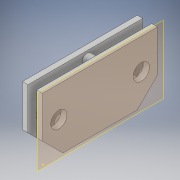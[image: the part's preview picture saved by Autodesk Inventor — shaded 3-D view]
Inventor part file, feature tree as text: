
AUTODESK INVENTOR PART (.ipt)
format: ipt  version: 2017 (Build 210142000, 142)  size: 175,616 bytes
history: native  units: in
note: dims shown in document units (in); Inventor stores cm internally (conversion verified against a paired STEP export)
features: sketch x6, extrude x5, chamfer x2, hole x2, plane x1, thicken_offset x1
ambient origin geometry x8: Origin, YZ Plane, XZ Plane, XY Plane, X Axis, Y Axis, Z Axis, Center Point
bodies: Solid1 (feature_tree)
feature tree (17):
  extrude  "Extrusion1"  Depth=0.125in TaperAngle=45.0deg
  chamfer  "Chamfer1"  Distance=0.125in Angle=45.0deg
  chamfer  "Chamfer2"  Distance=10.0in
  extrude  "Extrusion2"  Depth=0.125in TaperAngle=0.0deg
  plane  "Work Plane1"
  extrude  "Extrusion3"  Depth=0.125in
  extrude  "Extrusion4"  Depth=0.125in TaperAngle=0.0deg
  thicken_offset  "Thicken1"
  extrude  "Extrusion5"  Depth=1.0in
  hole  "Hole4"  [1 undecoded]
  sketch  "Sketch6"  dims[d55=0.19in d56=0.1in d57=0.1in d58=0.75in d59=0.375in d60=0.25in d61=0.5635in d62=1.0in d63=0.8108in d8=1.0in d9=1.0in d37=1.0in d38=1.0in]
  hole  "Hole5"  [1 undecoded]
  sketch  "Sketch1"  dims[d0=0.125in d1=0.0in d2=0.125in d3=0.125in d4=45.0deg d5=0.125in d6=0.125in d7=45.0deg d26=10.0in d27=0.0in]
  sketch  "Sketch2"  dims[d28=0.001in d29=0.125in d30=0.0in]
  sketch  "Sketch3"  dims[d31=0.125in d32=0.0in d33=0.001in]
  sketch  "Sketch4"  dims[d34=0.001in d35=0.125in d36=0.0in]
  sketch  "Sketch5"  dims[d46=0.19in d47=0.1in d48=0.1in d49=0.75in d50=0.375in d51=0.25in d52=0.5635in d53=1.0in d54=0.8108in]
note: 2 required parameter values undecoded (feature->parameter linkage not recoverable at this tier; creation-order binding heuristic only, values carry confidence <= 0.55)
